# Revit family: IS_Tesi_Multiproduct_BIM_IT_T3541;T3542
name_source: partatom
category: Plumbing Fixtures
revit_build: Autodesk Revit MEP 2014 (Build: 20130308_1515(x64)
units: mm (PartAtom-declared; Revit-internal decimal feet)

## types (2) — shared parameters
Accessori = www.idealstandard.it
AltezzaNominale = 400 mm
Assembly Code = C1030200
Autore = Ideal Standard Italia
Brand = Ideal Standard
Caratteristiche = ﻿Vaso sospeso a cacciata con scarico a parete e fissaggi completamente nascosti. Completo di sedile slim a sgancio rapido. Per il fissaggio a parete è necessario utilizzare l’apposito kit TT0299327 incluso nella confezione ed il sostegno metallico T655067 da ordinare separatamente. Certificato per scarico 4,5/3 litri.
Colore = Bianco
Connessione = Installazione
Default Elevation = 400 mm
DescrizioneClassifcazioneUni2015 = WC pans
Dimensione = 400 x 535 x 365 mm
DurataGaranziaProdotti = 99
Finitura = Bianco
Garanzia = Garanzia Idealstandard
IfcEsportaCome = IfcSanitaryTerminalType
InformaziniGaranzia = www.idealstandard.it/garanzia.html
InformazioniDiProdotto = www.idealstandard.it/prodotti/html
InformazioniGaranzia = www.idealstandard.it/garanzia.html
InstruzioniInstallazione = www.idealstandard.it/prodotti/html
LarghezzaNominale = 365 mm  [stored 1.19751 ft]
LunghezzaNominale = 535 mm  [stored 1.75525 ft]
Materiale = Porcellana Vetrificata (Vitreous China)
PesoNetto = 23,15 KG
Produttore = www.idealstandard.it
ProfonditaNominale = 535 mm  [stored 1.75525 ft]
Revisione = 1
RiferimentoClassificazioneUni2015 = Pr_40_20_93_94
Spazio = interno
Telefono = 800 652 290
TipoEspotazioneIfc = WCPANS
URL = www.idealstandard.it
UnitàDurata = anni
UnitàDurataGaranzia = anni
UnitàVolume = Litri
VersioneClassificazioneUni2015 = Products v1.1
zero-valued in all types: Cost, CostoDiSostituzione, ProfonditàNominale, SpilloverLivello, WFU

## per-type parameters (varying)
| type | CodiceABarre | Description | Model | Nome | NomeOggettoBim | NumeroDiModello |
| T354201 -TESI WH BOWL WHITE B.RIM HF BXD SWNC S&C | 8014140430469 | TESI WH BOWL WHITE B.RIM HF BXD SWNC S&C | T354201 | WcPans_TESI_T354201_IdealStandard | ISI_IdealStandard_WcPans_TESI_T354201 | T354201 |
| T354101 -TESI WH BOWL WHITE B.RIM HF BXD SWSC S&C | 8014140430452 | TESI WH BOWL WHITE B.RIM HF BXD SWSC S&C | T354101 | WcPans_TESI_T354101_IdealStandard | ISI_IdealStandard_WcPans_TESI_T354101 | T354101 |

note: [stored X ft] marks values corroborated as IEEE doubles in the binary element streams (Revit-internal decimal feet)

## geometry (parser evidence)
native form markers: Sweep x2
no freeform markers — native parametric forms only
